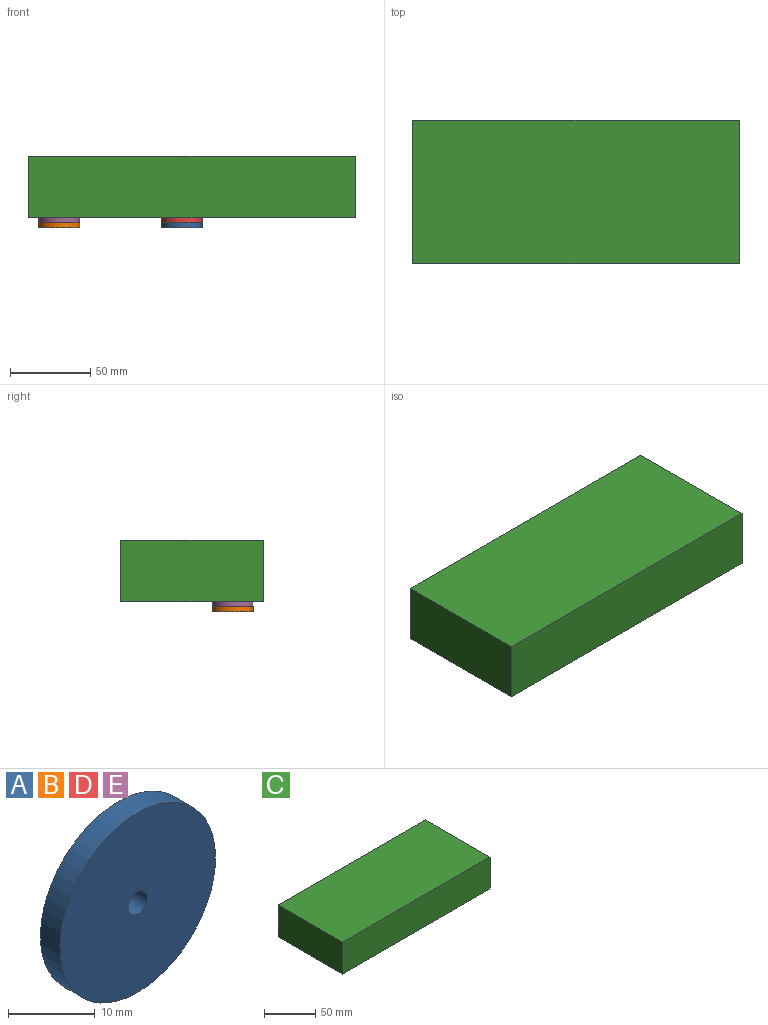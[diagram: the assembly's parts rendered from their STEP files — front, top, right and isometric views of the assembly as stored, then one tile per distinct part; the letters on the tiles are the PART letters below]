
ASSEMBLY  parts=5 mates=4
PART A: 4 faces, bbox 25.4x3.2x25.4 mm
  f0: cylinder r=1.59mm len=3.18mm, axis (0,1,0), area 31.7mm2, adj f2,f3
  f1: cylinder r=12.7mm len=25.4mm, axis (0,1,0), area 253.4mm2, adj f2,f3
  f2: plane 25.4x25.4mm, normal (0,-1,0), area 498.8mm2, adj f0,f1
  f3: plane 25.4x25.4mm, normal (0,1,0), area 498.8mm2, adj f0,f1
PART B: same geometry as A
PART C: 6 faces, bbox 203.2x88.9x38.1 mm
  f0: plane 203.2x38.1mm, normal (0,1,0), area 7741.9mm2, adj f1,f3,f4,f5
  f1: plane 203.2x88.9mm, normal (0,0,1), area 18064.5mm2, adj f0,f2,f4,f5
  f2: plane 203.2x38.1mm, normal (0,-1,0), area 7741.9mm2, adj f1,f3,f4,f5
  f3: plane 203.2x88.9mm, normal (0,0,-1), area 18064.5mm2, adj f0,f2,f4,f5
  f4: plane 88.9x38.1mm, normal (1,0,0), area 3387.1mm2, adj f0,f1,f2,f3
  f5: plane 88.9x38.1mm, normal (-1,0,0), area 3387.1mm2, adj f0,f1,f2,f3
PART D: same geometry as A
PART E: same geometry as A
PLACE A rot(axis=(-1,0,0),90deg) t=(-6.35,-25.4,-44.45)mm
PLACE B rot(axis=(-0.14,0.7,-0.7),164.1deg) t=(-82.55,-25.4,-44.45)mm
PLACE C t=(-101.6,0,-19.05)mm
PLACE D rot(axis=(1,0,0),90deg) t=(-6.35,-25.4,-38.1)mm
PLACE E rot(axis=(1,0,0),90deg) t=(-82.55,-25.4,-38.1)mm
MATE fastened E.f1 <-> C.f3  axis (0,0,1) through (-82.55,-25.4,-38.1)mm
MATE revolute E.f1 <-> B.f1  axis (0,0,-1) through (-82.55,-25.4,-41.28)mm
MATE fastened D.f1 <-> C.f3  axis (0,0,1) through (-6.35,-25.4,-38.1)mm
MATE revolute A.f1 <-> D.f1  axis (0,0,1) through (-6.35,-25.4,-41.28)mm
